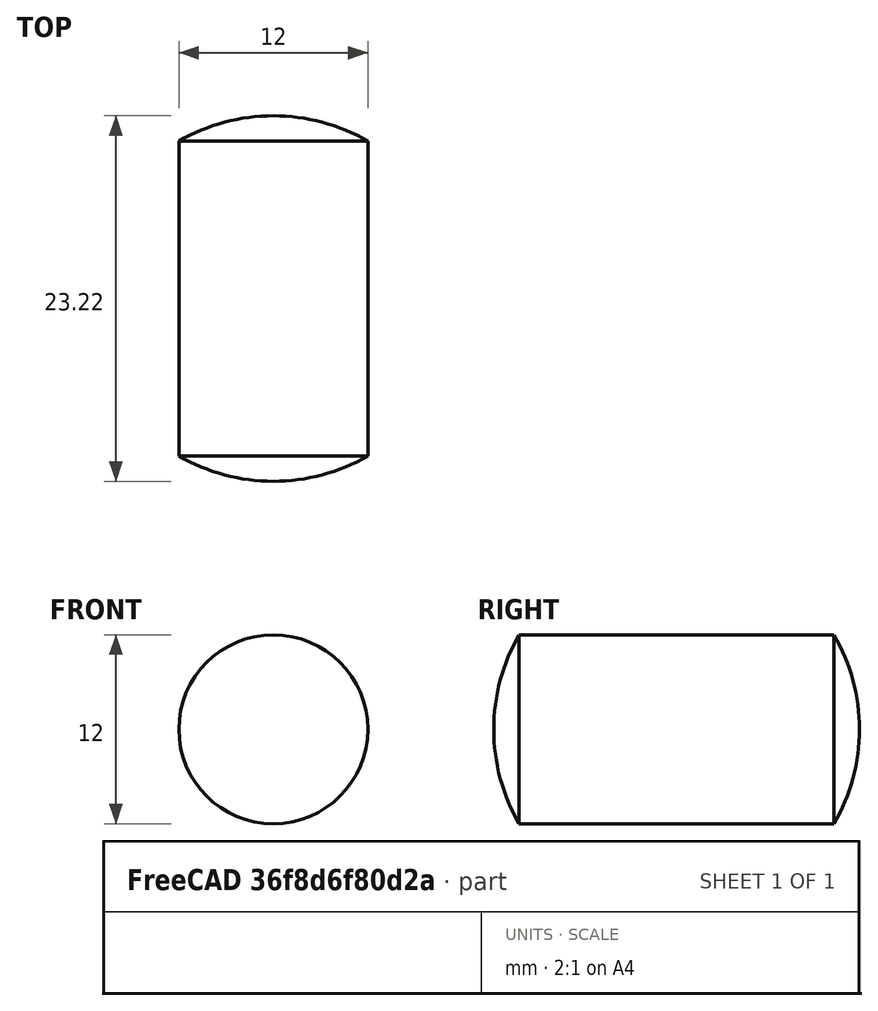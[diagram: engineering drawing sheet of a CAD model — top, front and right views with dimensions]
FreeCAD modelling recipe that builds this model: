
FCSTD DOCUMENT  (FreeCAD 0.15R4470 (Git))
Label: Zyl-Stift_DIN_7-12x20
License: CC-BY 3.0
LicenseURL: http://creativecommons.org/licenses/by/3.0/
objects: Sketcher::SketchObject×1, PartDesign::Revolution×1
note: 3 computed .brp shape members not serialized (recipe doc carries the construction recipe); baked Part::Feature solids carry a one-line shape summary decoded from their .brp

FEATURE [Sketcher::SketchObject] Sketch
  Placement = pos=(0,0,0) rot=(0.57735,0.57735,0.57735;2.0944rad)
  sketch-geometry (4):
    g0: ArcOfCircle CenterX=9.6077 CenterY=0 CenterZ=0 NormalX=0 NormalY=0 NormalZ=1 Radius=12 StartAngle=0 EndAngle=0.523599
    g1: LineSegment StartX=-4e-12 StartY=6 StartZ=0 EndX=20 EndY=6 EndZ=0
    g2: LineSegment StartX=-1.6077 StartY=0 StartZ=0 EndX=21.6077 EndY=0 EndZ=0
    g3: ArcOfCircle CenterX=10.3923 CenterY=0 CenterZ=0 NormalX=0 NormalY=0 NormalZ=1 Radius=12 StartAngle=2.61799 EndAngle=3.14159
  constraints (14):
    c: PointOnObject(g2,g-1)
    c: PointOnObject(g1,g-2)
    c: Coincident(g0,g1)
    c: PointOnObject(g0,g-1)
    c: Horizontal(g1)
    c: Coincident(g2,g0)
    c: Horizontal(g2)
    c: Radius(g0) = 12
    c: PointOnObject(g3,g2)
    c: Coincident(g3,g1)
    c: Coincident(g3,g2)
    c: Equal(g3,g0)
    c: DistanceY(g-1,g1) = 6
    c: DistanceX(g1) = 20
FEATURE [PartDesign::Revolution] Revolution  label="Zyl-Stift DIN 7-12x20 #"
  Angle = 360
  Axis = (0,1,0)
  Base = (0,0,0)
  Placement = pos=(0,0,0) rot=(0.57735,0.57735,0.57735;2.0944rad)
  ReferenceAxis = -> Sketch [H_Axis]
  Sketch = -> Sketch
